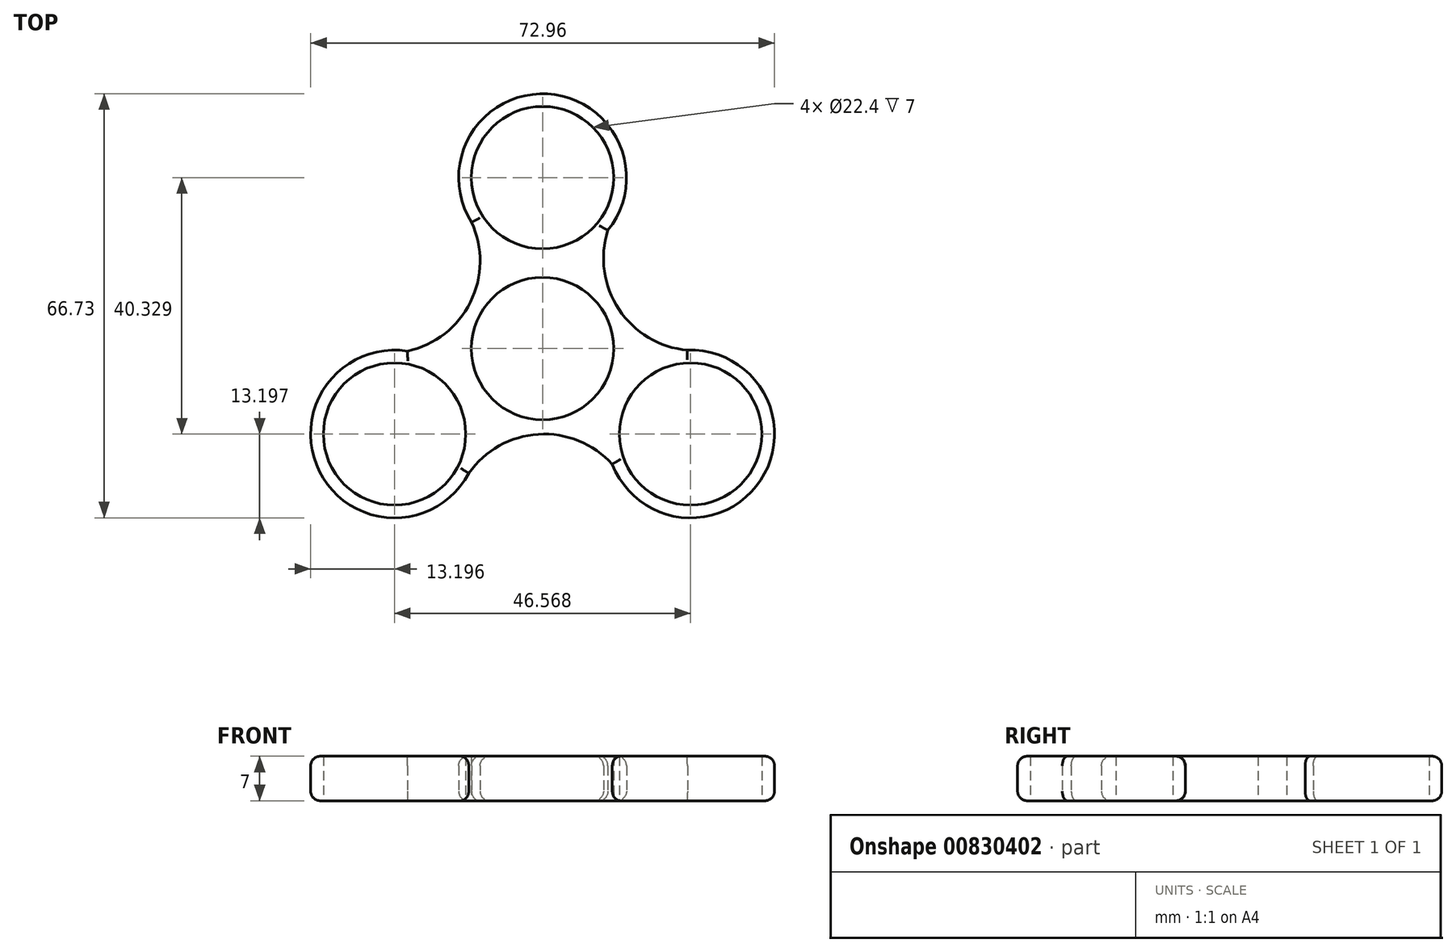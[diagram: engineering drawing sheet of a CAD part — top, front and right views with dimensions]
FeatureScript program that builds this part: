
annotation { "Feature Type Name" : "Feature", "Feature Type Description" : "" }
export const myFeature = defineFeature(function(context is Context, id is Id, definition is map)
    precondition{}
    {
        {
            var Q0;
            Q0=qCreatedBy(makeId("Top.planeOp"),FACE);
            var sketch = newSketch(context, id + "F0", { "sketchPlane" : qUnion([Q0])});
            skCircle(sketch, "E0", {"center": v(0, 0) * mm, "radius": 11.2 * mm});
            skCircle(sketch, "E1", {"center": v(0, 26.89) * mm, "radius": 11.2 * mm});
            skArc(sketch, "E2", {"start": v(10.27, 18.6) * mm, "mid": v(0.78, 40.06) * mm, "end": v(-11.17, 19.86) * mm});
            skArc(sketch, "E3.1.0", {"start": v(-21.24, -0.4) * mm, "mid": v(-35.08, -19.36) * mm, "end": v(-11.61, -19.6) * mm});
            skCircle(sketch, "E3.1.1", {"center": v(-23.28, -13.44) * mm, "radius": 11.2 * mm});
            skArc(sketch, "E3.2.0", {"start": v(10.97, -18.2) * mm, "mid": v(34.3, -20.7) * mm, "end": v(22.78, -0.25) * mm});
            skCircle(sketch, "E3.2.1", {"center": v(23.28, -13.44) * mm, "radius": 11.2 * mm});
            skArc(sketch, "E4", {"start": v(-21.24, -0.4) * mm, "mid": v(-11.35, 7.31) * mm, "end": v(-11.17, 19.86) * mm});
            skArc(sketch, "E5.1.0", {"start": v(10.97, -18.2) * mm, "mid": v(-0.66, -13.48) * mm, "end": v(-11.61, -19.6) * mm});
            skArc(sketch, "E5.2.0", {"start": v(10.27, 18.6) * mm, "mid": v(12, 6.17) * mm, "end": v(22.78, -0.25) * mm});
            skSolve(sketch);
        }
        {
            var Q0;
            Q0=makeQuery(id+"F0.imprint","IMPRINT",FACE,{"disambiguationData":[TD([[makeQuery(id+"F0.imprint","IMPRINT",EDGE,{"derivedFrom":sQuery(id+"F0.wireOp",EDGE,"E0")}),-1.0]])]});
            extrude(context, id + "F1", {"entities" : qUnion([Q0]), "depth" : 7 * mm, "offsetDistance" : 25 * mm});
        }
        {
            var Q0;
            Q0=makeQuery(id+"F1.opExtrude","CAP_EDGE",EDGE,{"disambiguationData":[OSD([sQuery(id+"F0.wireOp",EDGE,"E5.1.0")])],"isStart":false});
            var Q1;
            Q1=makeQuery(id+"F1.opExtrude","CAP_EDGE",EDGE,{"disambiguationData":[OSD([sQuery(id+"F0.wireOp",EDGE,"E5.1.0")])],"isStart":true});
            var Q2;
            Q2=makeQuery(id+"F1.opExtrude","CAP_EDGE",EDGE,{"disambiguationData":[OSD([sQuery(id+"F0.wireOp",EDGE,"E3.1.0")])],"isStart":false});
            var Q3;
            Q3=makeQuery(id+"F1.opExtrude","CAP_EDGE",EDGE,{"disambiguationData":[OSD([sQuery(id+"F0.wireOp",EDGE,"E4")])],"isStart":false});
            var Q4;
            Q4=makeQuery(id+"F1.opExtrude","CAP_EDGE",EDGE,{"disambiguationData":[OSD([sQuery(id+"F0.wireOp",EDGE,"E3.1.0")])],"isStart":true});
            var Q5;
            Q5=makeQuery(id+"F1.opExtrude","CAP_EDGE",EDGE,{"disambiguationData":[OSD([sQuery(id+"F0.wireOp",EDGE,"E4")])],"isStart":true});
            var Q6;
            Q6=makeQuery(id+"F1.opExtrude","CAP_EDGE",EDGE,{"disambiguationData":[OSD([sQuery(id+"F0.wireOp",EDGE,"E3.2.0")])],"isStart":false});
            var Q7;
            Q7=makeQuery(id+"F1.opExtrude","CAP_EDGE",EDGE,{"disambiguationData":[OSD([sQuery(id+"F0.wireOp",EDGE,"E5.2.0")])],"isStart":false});
            var Q8;
            Q8=makeQuery(id+"F1.opExtrude","CAP_EDGE",EDGE,{"disambiguationData":[OSD([sQuery(id+"F0.wireOp",EDGE,"E3.2.0")])],"isStart":true});
            var Q9;
            Q9=makeQuery(id+"F1.opExtrude","CAP_EDGE",EDGE,{"disambiguationData":[OSD([sQuery(id+"F0.wireOp",EDGE,"E5.2.0")])],"isStart":true});
            var Q10;
            Q10=makeQuery(id+"F1.opExtrude","CAP_EDGE",EDGE,{"disambiguationData":[OSD([sQuery(id+"F0.wireOp",EDGE,"E2")])],"isStart":false});
            var Q11;
            Q11=makeQuery(id+"F1.opExtrude","CAP_EDGE",EDGE,{"disambiguationData":[OSD([sQuery(id+"F0.wireOp",EDGE,"E2")])],"isStart":true});
            fillet(context, id + "F2", {"entities" : qUnion([Q0, Q1, Q2, Q3, Q4, Q5, Q6, Q7, Q8, Q9, Q10, Q11]), "radius" : 1.5 * mm, "tangentPropagation" : true, "allowEdgeOverflow" : false});
        }
    });
